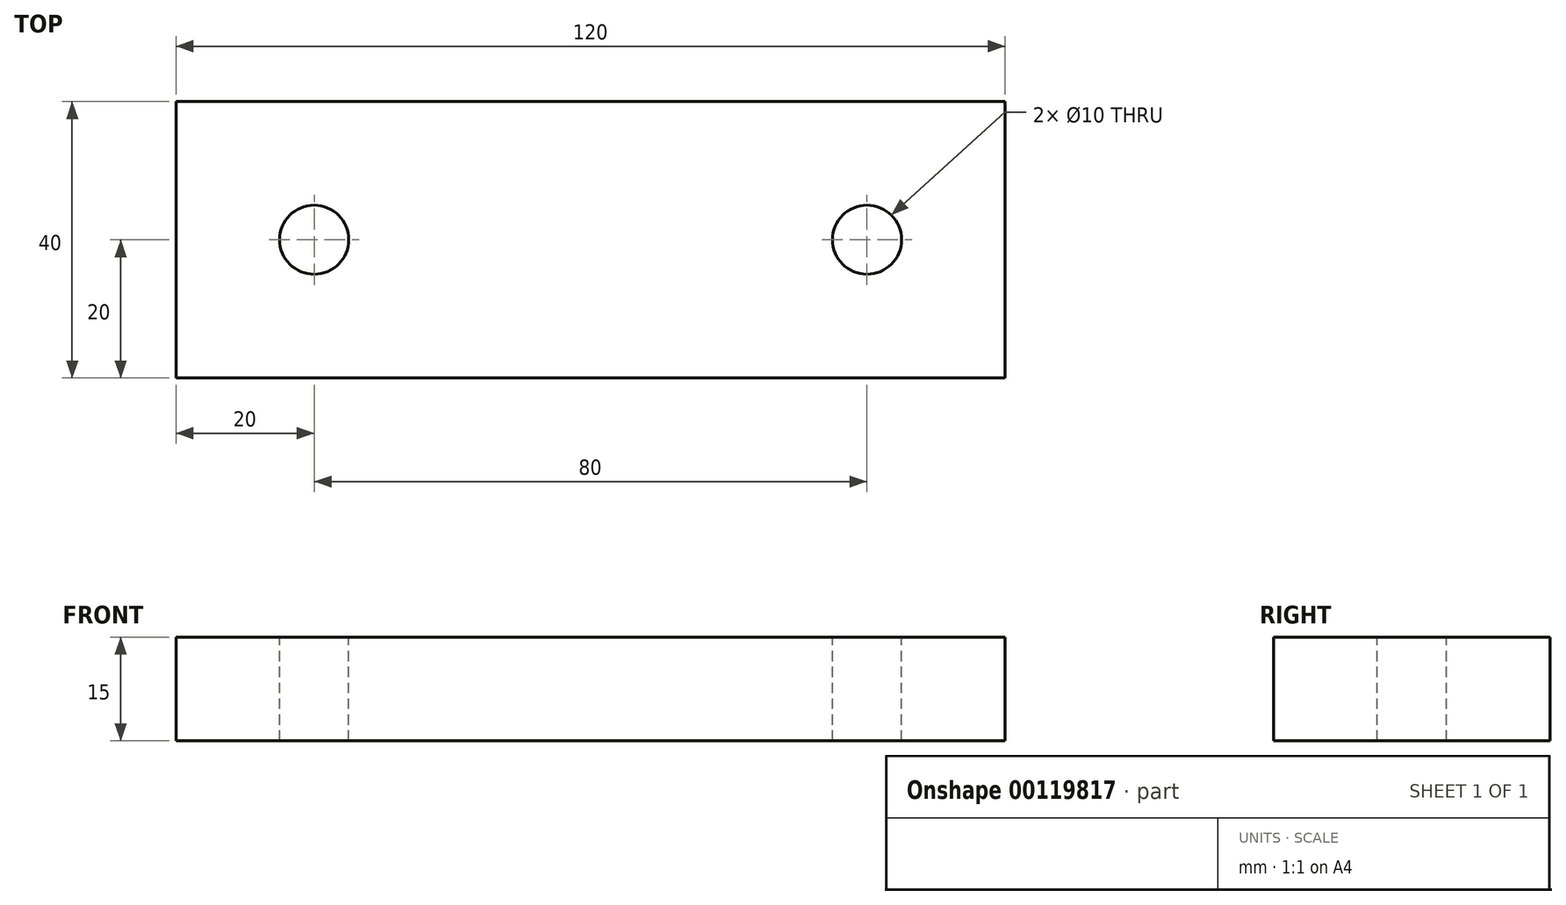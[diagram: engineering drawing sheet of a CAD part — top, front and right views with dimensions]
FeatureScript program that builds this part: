
annotation { "Feature Type Name" : "Feature", "Feature Type Description" : "" }
export const myFeature = defineFeature(function(context is Context, id is Id, definition is map)
    precondition{}
    {
        {
            var Q0;
            Q0=qCreatedBy(makeId("Top.planeOp"),FACE);
            var sketch = newSketch(context, id + "F0", { "sketchPlane" : qUnion([Q0])});
            skLineSegment(sketch, "E0.bottom", {"start": v(0, 0) * mm, "end": v(120, 0) * mm});
            skLineSegment(sketch, "E0.top", {"start": v(0, 40) * mm, "end": v(120, 40) * mm});
            skLineSegment(sketch, "E0.left", {"start": v(0, 0) * mm, "end": v(0, 40) * mm});
            skLineSegment(sketch, "E0.right", {"start": v(120, 0) * mm, "end": v(120, 40) * mm});
            skLineSegment(sketch, "E1", {"start": v(-26.23, 20) * mm, "end": v(171.4, 20) * mm, "construction": true});
            skSolve(sketch);
        }
        {
            var Q0;
            Q0 = qSketchRegion(id + "F0", true);
            extrude(context, id + "F1", {"entities" : qUnion([Q0]), "depth" : 15 * mm});
        }
        {
            var Q0;
            Q0=makeQuery(id+"F1.opExtrude","CAP_FACE",FACE,{"disambiguationData":[OSD([sQuery(id+"F0.wireOp",EDGE,"E0.bottom"),sQuery(id+"F0.wireOp",EDGE,"E0.top"),sQuery(id+"F0.wireOp",EDGE,"E0.left"),sQuery(id+"F0.wireOp",EDGE,"E0.right")])],"isStart":false});
            var sketch = newSketch(context, id + "F2", { "sketchPlane" : qUnion([Q0])});
            skCircle(sketch, "E2", {"center": v(20, 20) * mm, "radius": 5 * mm});
            skCircle(sketch, "E3", {"center": v(100, 20) * mm, "radius": 5 * mm});
            skSolve(sketch);
        }
        {
            var Q0;
            Q0=makeQuery(id+"F2.imprint","IMPRINT",FACE,{"disambiguationData":[TD([[makeQuery(id+"F2.imprint","IMPRINT",EDGE,{"derivedFrom":sQuery(id+"F2.wireOp",EDGE,"E2")}),1.0]])]});
            var Q1;
            Q1=makeQuery(id+"F2.imprint","IMPRINT",FACE,{"disambiguationData":[TD([[makeQuery(id+"F2.imprint","IMPRINT",EDGE,{"derivedFrom":sQuery(id+"F2.wireOp",EDGE,"E3")}),1.0]])]});
            extrude(context, id + "F3", {"entities" : qUnion([Q0, Q1]), "operationType" : NewBodyOperationType.REMOVE, "endBound" : BoundingType.THROUGH_ALL, "oppositeDirection" : true, "depth" : 25 * mm});
        }
    });
